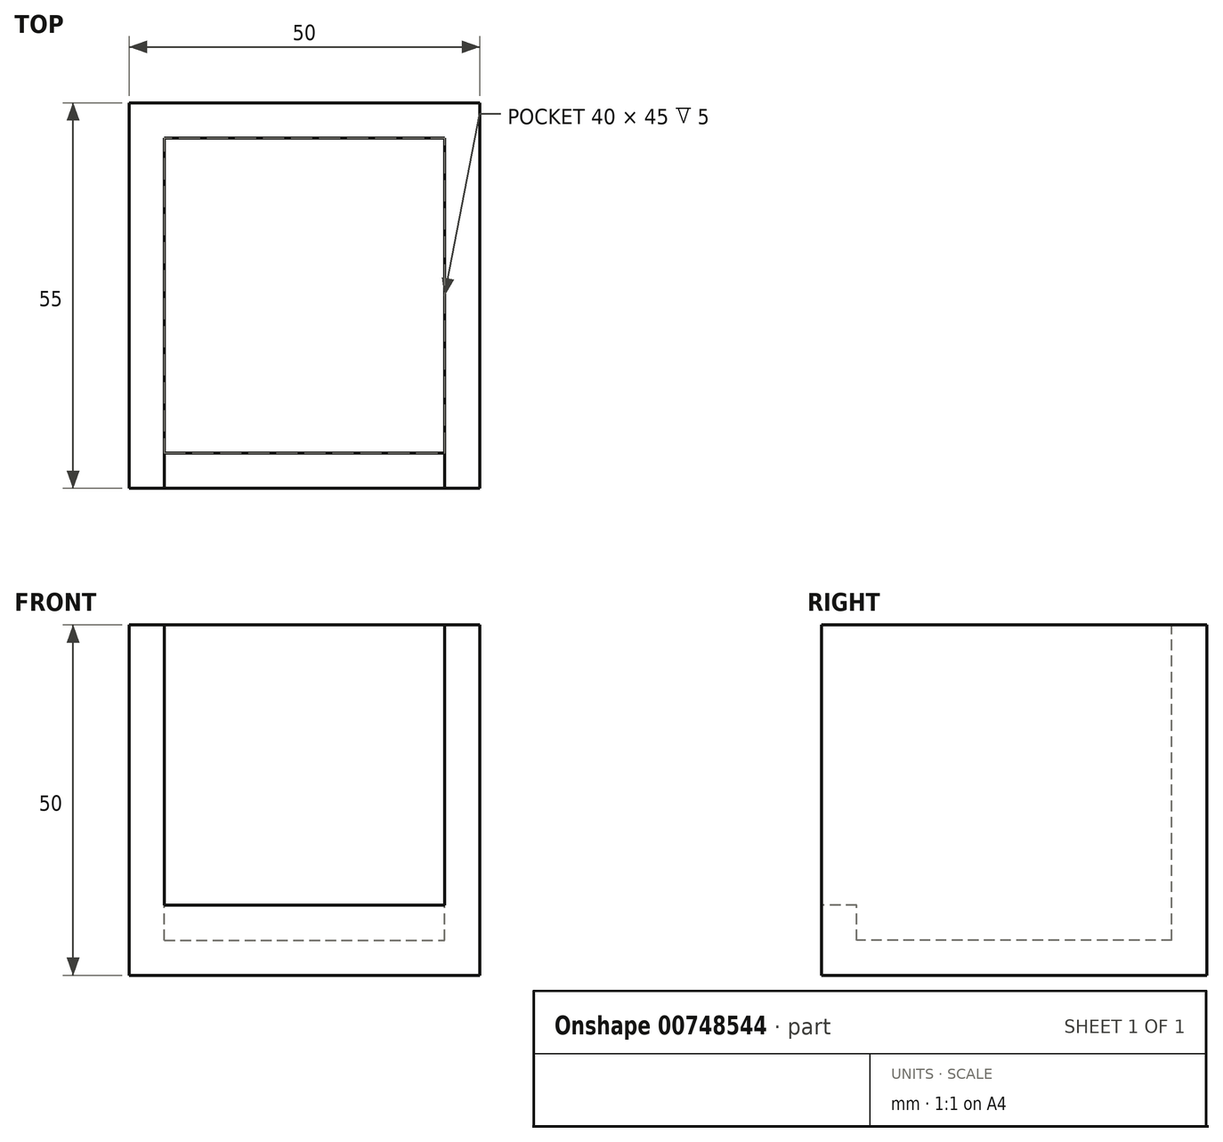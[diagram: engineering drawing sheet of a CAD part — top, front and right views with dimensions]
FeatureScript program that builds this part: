
annotation { "Feature Type Name" : "Feature", "Feature Type Description" : "" }
export const myFeature = defineFeature(function(context is Context, id is Id, definition is map)
    precondition{}
    {
        {
            var Q0;
            Q0=qCreatedBy(makeId("Top.planeOp"),FACE);
            var sketch = newSketch(context, id + "F0", { "sketchPlane" : qUnion([Q0])});
            skLineSegment(sketch, "E0.bottom", {"start": v(-25, 27.5) * mm, "end": v(25, 27.5) * mm});
            skLineSegment(sketch, "E0.top", {"start": v(-25, -27.5) * mm, "end": v(25, -27.5) * mm});
            skLineSegment(sketch, "E0.left", {"start": v(-25, 27.5) * mm, "end": v(-25, -27.5) * mm});
            skLineSegment(sketch, "E0.right", {"start": v(25, 27.5) * mm, "end": v(25, -27.5) * mm});
            skPoint(sketch, "E0.middle", {"position": v(0, 0) * mm});
            skSolve(sketch);
        }
        {
            var Q0;
            Q0 = qSketchRegion(id + "F0", true);
            extrude(context, id + "F1", {"entities" : qUnion([Q0]), "depth" : 50 * mm, "offsetDistance" : 25 * mm});
        }
        {
            var Q0;
            Q0=makeQuery(id+"F1.opExtrude","CAP_FACE",FACE,{"disambiguationData":[OSD([sQuery(id+"F0.wireOp",EDGE,"E0.bottom"),sQuery(id+"F0.wireOp",EDGE,"E0.top"),sQuery(id+"F0.wireOp",EDGE,"E0.left"),sQuery(id+"F0.wireOp",EDGE,"E0.right")])],"isStart":false});
            var sketch = newSketch(context, id + "F2", { "sketchPlane" : qUnion([Q0])});
            skLineSegment(sketch, "E1.bottom", {"start": v(-20, 22.5) * mm, "end": v(20, 22.5) * mm});
            skLineSegment(sketch, "E1.top", {"start": v(-20, -22.5) * mm, "end": v(20, -22.5) * mm});
            skLineSegment(sketch, "E1.left", {"start": v(-20, 22.5) * mm, "end": v(-20, -22.5) * mm});
            skLineSegment(sketch, "E1.right", {"start": v(20, 22.5) * mm, "end": v(20, -22.5) * mm});
            skPoint(sketch, "E1.middle", {"position": v(0, 0) * mm});
            skSolve(sketch);
        }
        {
            var Q0;
            Q0 = qSketchRegion(id + "F2", true);
            extrude(context, id + "F3", {"entities" : qUnion([Q0]), "operationType" : NewBodyOperationType.REMOVE, "oppositeDirection" : true, "depth" : 45 * mm, "offsetDistance" : 25 * mm});
        }
        {
            var Q0;
            Q0=makeQuery(id+"F1.opExtrude","SWEPT_FACE",FACE,{"disambiguationData":[OSD([sQuery(id+"F0.wireOp",EDGE,"E0.top")])]});
            var sketch = newSketch(context, id + "F4", { "sketchPlane" : qUnion([Q0])});
            skLineSegment(sketch, "E2.bottom", {"start": v(20, 10) * mm, "end": v(-20, 10) * mm});
            skLineSegment(sketch, "E2.top", {"start": v(20, 50) * mm, "end": v(-20, 50) * mm});
            skLineSegment(sketch, "E2.left", {"start": v(20, 10) * mm, "end": v(20, 50) * mm});
            skLineSegment(sketch, "E2.right", {"start": v(-20, 10) * mm, "end": v(-20, 50) * mm});
            skPoint(sketch, "E2.middle", {"position": v(0, 30) * mm});
            skSolve(sketch);
        }
        {
            var Q0;
            Q0 = qSketchRegion(id + "F4", true);
            extrude(context, id + "F5", {"entities" : qUnion([Q0]), "operationType" : NewBodyOperationType.REMOVE, "oppositeDirection" : true, "depth" : 5 * mm, "offsetDistance" : 25 * mm});
        }
    });
